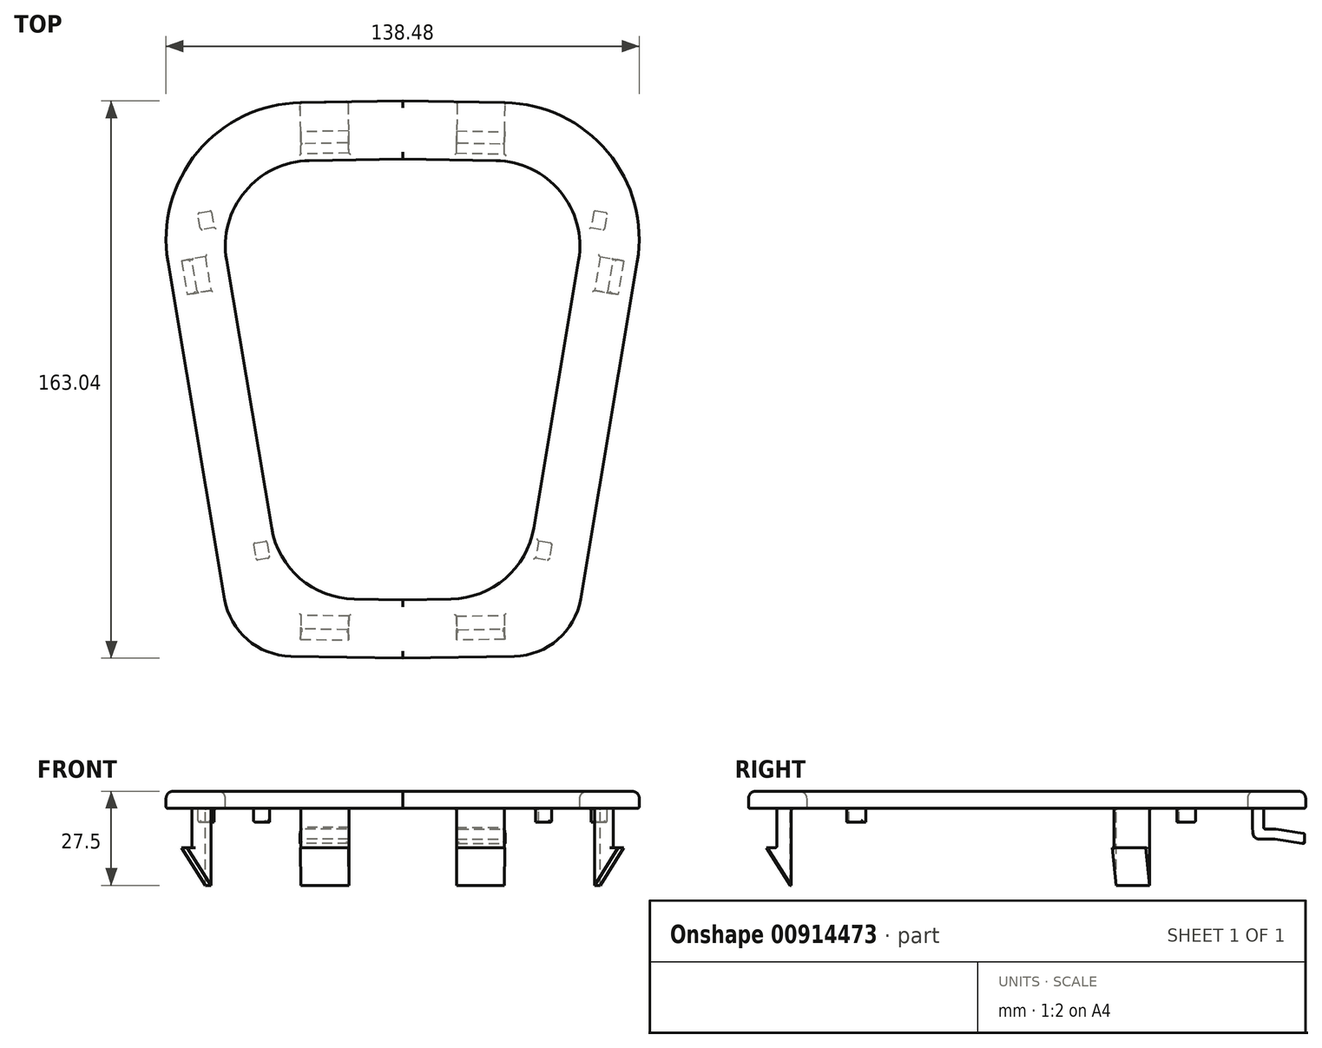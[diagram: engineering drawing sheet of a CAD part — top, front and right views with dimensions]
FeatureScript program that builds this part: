
annotation { "Feature Type Name" : "Feature", "Feature Type Description" : "" }
export const myFeature = defineFeature(function(context is Context, id is Id, definition is map)
    precondition{}
    {
        {
            var Q0;
            Q0=qCreatedBy(makeId("Top.planeOp"),FACE);
            var sketch = newSketch(context, id + "F0", { "sketchPlane" : qUnion([Q0])});
            skLineSegment(sketch, "E0", {"start": v(0, 81.52) * mm, "end": v(0, -81.52) * mm, "construction": true});
            skLineSegment(sketch, "E1", {"start": v(0, 81.52) * mm, "end": v(76.4, 80.19) * mm});
            skLineSegment(sketch, "E2", {"start": v(76.4, 80.19) * mm, "end": v(49.33, -80.66) * mm});
            skLineSegment(sketch, "E3", {"start": v(49.33, -80.66) * mm, "end": v(0, -81.52) * mm});
            skLineSegment(sketch, "E4", {"start": v(0, 81.52) * mm, "end": v(0, -81.52) * mm});
            skLineSegment(sketch, "E5.0", {"start": v(65.28, 80.38) * mm, "end": v(38.15, -80.86) * mm, "construction": true});
            skLineSegment(sketch, "E6", {"start": v(57.8, 35.9) * mm, "end": v(68.64, 34.08) * mm});
            skLineSegment(sketch, "E7", {"start": v(56.13, 26.04) * mm, "end": v(66.98, 24.22) * mm});
            skLineSegment(sketch, "E8", {"start": v(57.8, 35.9) * mm, "end": v(56.13, 26.04) * mm});
            skLineSegment(sketch, "E9", {"start": v(68.64, 34.08) * mm, "end": v(66.98, 24.22) * mm});
            skLineSegment(sketch, "E10", {"start": v(0, 66.52) * mm, "end": v(73.88, 65.23) * mm, "construction": true});
            skLineSegment(sketch, "E11", {"start": v(29.74, 66) * mm, "end": v(30, 81) * mm});
            skLineSegment(sketch, "E12", {"start": v(15.74, 66.24) * mm, "end": v(16, 81.24) * mm});
            skLineSegment(sketch, "E13", {"start": v(15.74, 66.24) * mm, "end": v(29.74, 66) * mm});
            skLineSegment(sketch, "E14", {"start": v(16, 81.24) * mm, "end": v(30, 81) * mm});
            skLineSegment(sketch, "E15", {"start": v(0, -69.52) * mm, "end": v(51.36, -68.62) * mm, "construction": true});
            skLineSegment(sketch, "E16", {"start": v(15.74, -69.25) * mm, "end": v(15.95, -81.24) * mm});
            skLineSegment(sketch, "E17", {"start": v(15.74, -69.25) * mm, "end": v(29.74, -69) * mm});
            skLineSegment(sketch, "E18", {"start": v(29.74, -69) * mm, "end": v(29.95, -81) * mm});
            skLineSegment(sketch, "E19", {"start": v(29.95, -81) * mm, "end": v(15.95, -81.24) * mm});
            skLineSegment(sketch, "E20", {"start": v(59.12, 43.8) * mm, "end": v(69.97, 41.97) * mm});
            skLineSegment(sketch, "E21", {"start": v(59.12, 43.8) * mm, "end": v(59.95, 48.73) * mm});
            skLineSegment(sketch, "E22", {"start": v(59.95, 48.73) * mm, "end": v(70.8, 46.9) * mm});
            skLineSegment(sketch, "E23", {"start": v(70.8, 46.9) * mm, "end": v(69.97, 41.97) * mm});
            skLineSegment(sketch, "E24", {"start": v(43.69, -47.92) * mm, "end": v(54.54, -49.74) * mm});
            skLineSegment(sketch, "E25", {"start": v(43.69, -47.92) * mm, "end": v(42.86, -52.85) * mm});
            skLineSegment(sketch, "E26", {"start": v(42.86, -52.85) * mm, "end": v(53.7, -54.67) * mm});
            skLineSegment(sketch, "E27", {"start": v(53.7, -54.67) * mm, "end": v(54.54, -49.74) * mm});
            skLineSegment(sketch, "E28.0", {"start": v(69.32, 80.31) * mm, "end": v(42.21, -80.78) * mm, "construction": true});
            skLineSegment(sketch, "E29.0", {"start": v(0, 69.52) * mm, "end": v(74.39, 68.22) * mm, "construction": true});
            skLineSegment(sketch, "E30.0", {"start": v(34.91, -63.9) * mm, "end": v(0, -64.52) * mm});
            skLineSegment(sketch, "E30.1", {"start": v(56.36, 63.54) * mm, "end": v(34.91, -63.9) * mm});
            skLineSegment(sketch, "E30.2", {"start": v(0, 64.52) * mm, "end": v(56.36, 63.54) * mm});
            skLineSegment(sketch, "E31", {"start": v(60.08, 25.38) * mm, "end": v(61.74, 35.24) * mm});
            skLineSegment(sketch, "E32", {"start": v(59.95, 48.73) * mm, "end": v(56, 49.39) * mm});
            skLineSegment(sketch, "E33", {"start": v(56, 49.39) * mm, "end": v(55.18, 44.46) * mm});
            skLineSegment(sketch, "E34", {"start": v(55.18, 44.46) * mm, "end": v(59.12, 43.8) * mm});
            skLineSegment(sketch, "E35", {"start": v(43.69, -47.92) * mm, "end": v(39.74, -47.25) * mm});
            skLineSegment(sketch, "E36", {"start": v(39.74, -47.25) * mm, "end": v(38.91, -52.18) * mm});
            skLineSegment(sketch, "E37", {"start": v(38.91, -52.18) * mm, "end": v(42.86, -52.85) * mm});
            skLineSegment(sketch, "E38", {"start": v(0, -73.52) * mm, "end": v(50.68, -72.64) * mm, "construction": true});
            skLineSegment(sketch, "E39", {"start": v(15.8, -73.24) * mm, "end": v(29.8, -73) * mm});
            skLineSegment(sketch, "E40", {"start": v(15.8, 69.24) * mm, "end": v(29.8, 69) * mm});
            skLineSegment(sketch, "E41", {"start": v(-105.5, -148.71) * mm, "end": v(-104.92, -148.71) * mm});
            skLineSegment(sketch, "E42", {"start": v(-104.92, -148.71) * mm, "end": v(-104.92, 145.13) * mm, "construction": true});
            skPoint(sketch, "E43", {"position": v(-104.92, 80.88) * mm});
            skPoint(sketch, "E44", {"position": v(-104.92, -81.12) * mm});
            skSolve(sketch);
        }
        {
            var Q0;
            {var subQ6=sQuery(id+"F0.wireOp",EDGE,"E8");Q0=makeQuery(id+"F0.imprint","IMPRINT",FACE,{"disambiguationData":[TD([[makeQuery(id+"F0.imprint","IMPRINT",EDGE,{"derivedFrom":subQ6}),-1.0]])]});}
            var Q1;
            {var subQ5=sQuery(id+"F0.wireOp",EDGE,"E40");var subQ8=makeQuery(id+"F0.imprint","IMPRINT",EDGE,{"derivedFrom":subQ5});var subQ9=sQuery(id+"F0.wireOp",EDGE,"E13");Q1=qUnion([makeQuery(id+"F0.imprint","IMPRINT",FACE,{"disambiguationData":[TD([[makeQuery(id+"F0.imprint","IMPRINT",EDGE,{"derivedFrom":subQ9}),1.0]])]}),makeQuery(id+"F0.imprint","IMPRINT",FACE,{"disambiguationData":[TD([[subQ8,1.0]])]})]);}
            var Q2;
            {var subQ0=sQuery(id+"F0.wireOp",EDGE,"E20");Q2=makeQuery(id+"F0.imprint","IMPRINT",FACE,{"disambiguationData":[TD([[makeQuery(id+"F0.imprint","IMPRINT",EDGE,{"derivedFrom":subQ0}),1.0]])]});}
            var Q3;
            {var subQ5=sQuery(id+"F0.wireOp",EDGE,"E31");Q3=makeQuery(id+"F0.imprint","IMPRINT",FACE,{"disambiguationData":[TD([[makeQuery(id+"F0.imprint","IMPRINT",EDGE,{"derivedFrom":subQ5}),-1.0]])]});}
            var Q4;
            {var subQ0=sQuery(id+"F0.wireOp",EDGE,"E39");var subQ3=sQuery(id+"F0.wireOp",EDGE,"E17");var subQ4=makeQuery(id+"F0.imprint","IMPRINT",EDGE,{"derivedFrom":subQ0});Q4=qUnion([makeQuery(id+"F0.imprint","IMPRINT",FACE,{"disambiguationData":[TD([[subQ4,-1.0]])]}),makeQuery(id+"F0.imprint","IMPRINT",FACE,{"disambiguationData":[TD([[makeQuery(id+"F0.imprint","IMPRINT",EDGE,{"derivedFrom":subQ3}),-1.0]])]})]);}
            var Q5;
            {var subQ0=sQuery(id+"F0.wireOp",EDGE,"E24");Q5=makeQuery(id+"F0.imprint","IMPRINT",FACE,{"disambiguationData":[TD([[makeQuery(id+"F0.imprint","IMPRINT",EDGE,{"derivedFrom":subQ0}),-1.0]])]});}
            var Q6;
            Q6=makeQuery(id+"F0.imprint","IMPRINT",FACE,{"disambiguationData":[TD([[makeQuery(id+"F0.imprint","IMPRINT",EDGE,{"derivedFrom":sQuery(id+"F0.wireOp",EDGE,"E25")}),-1.0]])]});
            var Q7;
            Q7=makeQuery(id+"F0.imprint","IMPRINT",FACE,{"disambiguationData":[TD([[makeQuery(id+"F0.imprint","IMPRINT",EDGE,{"derivedFrom":sQuery(id+"F0.wireOp",EDGE,"E21")}),1.0]])]});
            var Q8;
            {var subQ2=sQuery(id+"F0.wireOp",EDGE,"E8");Q8=makeQuery(id+"F0.imprint","IMPRINT",FACE,{"disambiguationData":[TD([[makeQuery(id+"F0.imprint","IMPRINT",EDGE,{"derivedFrom":subQ2}),1.0]])]});}
            extrude(context, id + "F1", {"entities" : qUnion([Q0, Q1, Q2, Q3, Q4, Q5, Q6, Q7, Q8]), "depth" : 5 * mm, "offsetDistance" : 25 * mm});
        }
        {
            var Q0;
            {var subQ2=sQuery(id+"F0.wireOp",EDGE,"E17");Q0=makeQuery(id+"F0.imprint","IMPRINT",FACE,{"disambiguationData":[TD([[makeQuery(id+"F0.imprint","IMPRINT",EDGE,{"derivedFrom":subQ2}),-1.0]])]});}
            var Q1;
            {var subQ2=sQuery(id+"F0.wireOp",EDGE,"E8");Q1=makeQuery(id+"F0.imprint","IMPRINT",FACE,{"disambiguationData":[TD([[makeQuery(id+"F0.imprint","IMPRINT",EDGE,{"derivedFrom":subQ2}),1.0]])]});}
            extrude(context, id + "F2", {"entities" : qUnion([Q0, Q1]), "operationType" : NewBodyOperationType.ADD, "oppositeDirection" : true, "depth" : 11.5 * mm, "offsetDistance" : 25 * mm});
        }
        {
            var Q0;
            Q0=makeQuery(id+"F2.opExtrude","SWEPT_FACE",FACE,{"disambiguationData":[OSD([sQuery(id+"F0.wireOp",EDGE,"E16")])]});
            var sketch = newSketch(context, id + "F3", { "sketchPlane" : qUnion([Q0])});
            skLineSegment(sketch, "E45", {"start": v(69.5, -11.5) * mm, "end": v(76.5, -11.5) * mm});
            skLineSegment(sketch, "E46", {"start": v(76.5, -11.5) * mm, "end": v(69.5, -22.5) * mm});
            skLineSegment(sketch, "E47", {"start": v(69.5, -22.5) * mm, "end": v(69.5, -11.5) * mm});
            skSolve(sketch);
        }
        {
            var Q0;
            Q0 = qSketchRegion(id + "F3", true);
            var Q1;
            Q1=makeQuery(id+"F2.opExtrude","SWEPT_FACE",FACE,{"disambiguationData":[OSD([sQuery(id+"F0.wireOp",EDGE,"E18")])]});
            extrude(context, id + "F4", {"entities" : qUnion([Q0]), "operationType" : NewBodyOperationType.ADD, "endBound" : BoundingType.UP_TO_SURFACE, "oppositeDirection" : true, "depth" : 25 * mm, "endBoundEntityFace" : qUnion([Q1]), "offsetDistance" : 25 * mm});
        }
        {
            var Q0;
            Q0=makeQuery(id+"F2.opExtrude","SWEPT_FACE",FACE,{"disambiguationData":[OSD([sQuery(id+"F0.wireOp",EDGE,"E7")])]});
            var sketch = newSketch(context, id + "F5", { "sketchPlane" : qUnion([Q0])});
            skLineSegment(sketch, "E48", {"start": v(51.03, -11.5) * mm, "end": v(58.03, -11.5) * mm});
            skLineSegment(sketch, "E49", {"start": v(58.03, -11.5) * mm, "end": v(51.03, -22.5) * mm});
            skLineSegment(sketch, "E50", {"start": v(51.03, -22.5) * mm, "end": v(51.03, -11.5) * mm});
            skSolve(sketch);
        }
        {
            var Q0;
            Q0 = qSketchRegion(id + "F5", true);
            var Q1;
            Q1=makeQuery(id+"F2.opExtrude","SWEPT_FACE",FACE,{"disambiguationData":[OSD([sQuery(id+"F0.wireOp",EDGE,"E6")])]});
            extrude(context, id + "F6", {"entities" : qUnion([Q0]), "operationType" : NewBodyOperationType.ADD, "endBound" : BoundingType.UP_TO_SURFACE, "oppositeDirection" : true, "depth" : 25 * mm, "endBoundEntityFace" : qUnion([Q1]), "offsetDistance" : 25 * mm});
        }
        {
            var Q0;
            {var subQ2=sQuery(id+"F0.wireOp",EDGE,"E13");Q0=makeQuery(id+"F0.imprint","IMPRINT",FACE,{"disambiguationData":[TD([[makeQuery(id+"F0.imprint","IMPRINT",EDGE,{"derivedFrom":subQ2}),1.0]])]});}
            extrude(context, id + "F7", {"entities" : qUnion([Q0]), "operationType" : NewBodyOperationType.ADD, "oppositeDirection" : true, "depth" : 5.5 * mm, "offsetDistance" : 25 * mm});
        }
        {
            var Q0;
            Q0=makeQuery(id+"F7.opExtrude","SWEPT_FACE",FACE,{"disambiguationData":[OSD([sQuery(id+"F0.wireOp",EDGE,"E11")])]});
            var sketch = newSketch(context, id + "F8", { "sketchPlane" : qUnion([Q0])});
            skLineSegment(sketch, "E51", {"start": v(66.5, -5.5) * mm, "end": v(66.54, -7.03) * mm});
            skLineSegment(sketch, "E52", {"start": v(73, -9) * mm, "end": v(81.5, -10.35) * mm});
            skLineSegment(sketch, "E53", {"start": v(81.5, -10.35) * mm, "end": v(81.5, -7.35) * mm});
            skLineSegment(sketch, "E54", {"start": v(69.5, -5.5) * mm, "end": v(69.5, -5.5) * mm});
            skPoint(sketch, "E55.visualSharp", {"position": v(69.5, -6.59) * mm});
            skLineSegment(sketch, "E56", {"start": v(70, -6) * mm, "end": v(73, -6) * mm});
            skLineSegment(sketch, "E57", {"start": v(73, -6) * mm, "end": v(81.5, -7.35) * mm});
            skLineSegment(sketch, "E58", {"start": v(66.5, -5.5) * mm, "end": v(69.5, -5.5) * mm});
            skPoint(sketch, "E59.visualSharp", {"position": v(69.5, -6) * mm});
            skArc(sketch, "E59.filletArc", {"start": v(69.5, -5.5) * mm, "mid": v(69.66, -5.85) * mm, "end": v(70, -6) * mm});
            skLineSegment(sketch, "E60", {"start": v(73, -9) * mm, "end": v(68.54, -9) * mm});
            skPoint(sketch, "E61.visualSharp", {"position": v(66.57, -9) * mm});
            skArc(sketch, "E61.filletArc", {"start": v(66.54, -7.03) * mm, "mid": v(67.13, -8.43) * mm, "end": v(68.54, -9) * mm});
            skSolve(sketch);
        }
        {
            var Q0;
            Q0 = qSketchRegion(id + "F8", true);
            var Q1;
            Q1=makeQuery(id+"F7.opExtrude","SWEPT_FACE",FACE,{"disambiguationData":[OSD([sQuery(id+"F0.wireOp",EDGE,"E12")])]});
            extrude(context, id + "F9", {"entities" : qUnion([Q0]), "operationType" : NewBodyOperationType.ADD, "endBound" : BoundingType.UP_TO_SURFACE, "oppositeDirection" : true, "depth" : 25 * mm, "endBoundEntityFace" : qUnion([Q1]), "offsetDistance" : 25 * mm});
        }
        {
            var Q0;
            Q0=makeQuery(id+"F0.imprint","IMPRINT",FACE,{"disambiguationData":[TD([[makeQuery(id+"F0.imprint","IMPRINT",EDGE,{"derivedFrom":sQuery(id+"F0.wireOp",EDGE,"E25")}),-1.0]])]});
            var Q1;
            Q1=makeQuery(id+"F0.imprint","IMPRINT",FACE,{"disambiguationData":[TD([[makeQuery(id+"F0.imprint","IMPRINT",EDGE,{"derivedFrom":sQuery(id+"F0.wireOp",EDGE,"E21")}),1.0]])]});
            extrude(context, id + "F10", {"entities" : qUnion([Q0, Q1]), "operationType" : NewBodyOperationType.ADD, "oppositeDirection" : true, "depth" : 4 * mm, "offsetDistance" : 25 * mm});
        }
        {
            var Q0;
            Q0=makeQuery(id+"F1.opExtrude","SWEPT_EDGE",EDGE,{"disambiguationData":[OSD([sQuery(id+"F0.wireOp",EDGE,"E2"),sQuery(id+"F0.wireOp",EDGE,"E3")])]});
            fillet(context, id + "F11", {"entities" : qUnion([Q0]), "radius" : 20 * mm, "tangentPropagation" : true, "allowEdgeOverflow" : false});
        }
        {
            var Q0;
            Q0=makeQuery(id+"F1.opExtrude","SWEPT_EDGE",EDGE,{"disambiguationData":[OSD([sQuery(id+"F0.wireOp",EDGE,"E1"),sQuery(id+"F0.wireOp",EDGE,"E2")])]});
            fillet(context, id + "F12", {"entities" : qUnion([Q0]), "radius" : 40 * mm, "tangentPropagation" : true, "allowEdgeOverflow" : false});
        }
        {
            var Q0;
            Q0=makeQuery(id+"F1.opExtrude","SWEPT_EDGE",EDGE,{"disambiguationData":[OSD([sQuery(id+"F0.wireOp",EDGE,"E30.0"),sQuery(id+"F0.wireOp",EDGE,"E30.1")])]});
            var Q1;
            Q1=makeQuery(id+"F1.opExtrude","SWEPT_EDGE",EDGE,{"disambiguationData":[OSD([sQuery(id+"F0.wireOp",EDGE,"E30.1"),sQuery(id+"F0.wireOp",EDGE,"E30.2")])]});
            fillet(context, id + "F13", {"entities" : qUnion([Q0, Q1]), "radius" : 25 * mm, "tangentPropagation" : true, "allowEdgeOverflow" : false});
        }
        {
            var Q0;
            Q0=makeQuery(id+"F1.opExtrude","SWEPT_BODY",BODY,{"disambiguationData":[OSD([sQuery(id+"F0.wireOp",EDGE,"E1"),sQuery(id+"F0.wireOp",EDGE,"E2"),sQuery(id+"F0.wireOp",EDGE,"E3"),sQuery(id+"F0.wireOp",EDGE,"E4"),sQuery(id+"F0.wireOp",EDGE,"E30.0"),sQuery(id+"F0.wireOp",EDGE,"E30.1"),sQuery(id+"F0.wireOp",EDGE,"E30.2")])]});
            var Q1;
            {var subQ0=sQuery(id+"F0.wireOp",EDGE,"E4");Q1=makeQuery(id+"F1.opExtrude","SWEPT_FACE",FACE,{"disambiguationData":[OSD([subQ0]),TDD([makeQuery(id+"F0.imprint","IMPRINT",EDGE,{"disambiguationData":[TD([[makeQuery(id+"F0.imprint","INTERSECT",VERTEX,{"derivedFrom":[subQ0,sQuery(id+"F0.wireOp",EDGE,"E30.2")]}),1.0]])],"derivedFrom":subQ0})])]});}
            mirror(context, id + "F14", {"operationType" : NewBodyOperationType.ADD, "entities" : qUnion([Q0]), "mirrorPlane" : qUnion([Q1])});
        }
        {
            var Q0;
            {var subQ0=makeQuery(id+"F1.opExtrude","CAP_FACE",FACE,{"disambiguationData":[OSD([sQuery(id+"F0.wireOp",EDGE,"E1"),sQuery(id+"F0.wireOp",EDGE,"E2"),sQuery(id+"F0.wireOp",EDGE,"E3"),sQuery(id+"F0.wireOp",EDGE,"E4"),sQuery(id+"F0.wireOp",EDGE,"E30.0"),sQuery(id+"F0.wireOp",EDGE,"E30.1"),sQuery(id+"F0.wireOp",EDGE,"E30.2")])],"isStart":false});Q0=makeQuery(id+"F14.boolean.opBoolean","MERGE",FACE,{"derivedFrom":[subQ0,makeQuery(id+"F14.opPattern","COPY",FACE,{"derivedFrom":subQ0,"instanceName":"1"})]});}
            fillet(context, id + "F15", {"entities" : qUnion([Q0]), "radius" : 2 * mm, "tangentPropagation" : true, "allowEdgeOverflow" : false});
        }
        {
            var Q0;
            {var subQ0=makeQuery(id+"F1.opExtrude","CAP_FACE",FACE,{"disambiguationData":[OSD([sQuery(id+"F0.wireOp",EDGE,"E1"),sQuery(id+"F0.wireOp",EDGE,"E2"),sQuery(id+"F0.wireOp",EDGE,"E3"),sQuery(id+"F0.wireOp",EDGE,"E4"),sQuery(id+"F0.wireOp",EDGE,"E30.0"),sQuery(id+"F0.wireOp",EDGE,"E30.1"),sQuery(id+"F0.wireOp",EDGE,"E30.2")])],"isStart":true});Q0=makeQuery(id+"F14.boolean.opBoolean","MERGE",FACE,{"derivedFrom":[subQ0,makeQuery(id+"F14.opPattern","COPY",FACE,{"derivedFrom":subQ0,"instanceName":"1"})]});}
            var Q1;
            Q1=makeQuery(id+"F14.opPattern","COPY",FACE,{"derivedFrom":makeQuery(id+"F2.opExtrude","SWEPT_FACE",FACE,{"disambiguationData":[OSD([sQuery(id+"F0.wireOp",EDGE,"E39")])]}),"instanceName":"1"});
            var Q2;
            Q2=makeQuery(id+"F2.opExtrude","SWEPT_FACE",FACE,{"disambiguationData":[OSD([sQuery(id+"F0.wireOp",EDGE,"E39")])]});
            var Q3;
            Q3=makeQuery(id+"F10.opExtrude","SWEPT_FACE",FACE,{"disambiguationData":[OSD([sQuery(id+"F0.wireOp",EDGE,"E25")])]});
            var Q4;
            Q4=makeQuery(id+"F2.opExtrude","SWEPT_FACE",FACE,{"disambiguationData":[OSD([sQuery(id+"F0.wireOp",EDGE,"E31")])]});
            var Q5;
            Q5=makeQuery(id+"F10.opExtrude","SWEPT_FACE",FACE,{"disambiguationData":[OSD([sQuery(id+"F0.wireOp",EDGE,"E21")])]});
            var Q6;
            Q6=makeQuery(id+"F10.opExtrude","SWEPT_FACE",FACE,{"disambiguationData":[OSD([sQuery(id+"F0.wireOp",EDGE,"E32")])]});
            var Q7;
            Q7=makeQuery(id+"F7.opExtrude","SWEPT_FACE",FACE,{"disambiguationData":[OSD([sQuery(id+"F0.wireOp",EDGE,"E40")])]});
            var Q8;
            Q8=makeQuery(id+"F9.opExtrude","SWEPT_FACE",FACE,{"disambiguationData":[OSD([sQuery(id+"F8.wireOp",EDGE,"E53")])]});
            var Q9;
            Q9=makeQuery(id+"F9.opExtrude","SWEPT_FACE",FACE,{"disambiguationData":[OSD([sQuery(id+"F8.wireOp",EDGE,"E57")])]});
            var Q10;
            Q10=makeQuery(id+"F14.opPattern","COPY",FACE,{"derivedFrom":makeQuery(id+"F7.opExtrude","SWEPT_FACE",FACE,{"disambiguationData":[OSD([sQuery(id+"F0.wireOp",EDGE,"E40")])]}),"instanceName":"1"});
            var Q11;
            Q11=makeQuery(id+"F14.opPattern","COPY",FACE,{"derivedFrom":makeQuery(id+"F9.opExtrude","SWEPT_FACE",FACE,{"disambiguationData":[OSD([sQuery(id+"F8.wireOp",EDGE,"E53")])]}),"instanceName":"1"});
            var Q12;
            Q12=makeQuery(id+"F14.opPattern","COPY",FACE,{"derivedFrom":makeQuery(id+"F9.opExtrude","SWEPT_FACE",FACE,{"disambiguationData":[OSD([sQuery(id+"F8.wireOp",EDGE,"E57")])]}),"instanceName":"1"});
            var Q13;
            Q13=makeQuery(id+"F14.opPattern","COPY",FACE,{"derivedFrom":makeQuery(id+"F10.opExtrude","SWEPT_FACE",FACE,{"disambiguationData":[OSD([sQuery(id+"F0.wireOp",EDGE,"E21")])]}),"instanceName":"1"});
            var Q14;
            Q14=makeQuery(id+"F14.opPattern","COPY",FACE,{"derivedFrom":makeQuery(id+"F10.opExtrude","SWEPT_FACE",FACE,{"disambiguationData":[OSD([sQuery(id+"F0.wireOp",EDGE,"E32")])]}),"instanceName":"1"});
            var Q15;
            Q15=makeQuery(id+"F14.opPattern","COPY",FACE,{"derivedFrom":makeQuery(id+"F2.opExtrude","SWEPT_FACE",FACE,{"disambiguationData":[OSD([sQuery(id+"F0.wireOp",EDGE,"E31")])]}),"instanceName":"1"});
            var Q16;
            Q16=makeQuery(id+"F14.opPattern","COPY",FACE,{"derivedFrom":makeQuery(id+"F10.opExtrude","SWEPT_FACE",FACE,{"disambiguationData":[OSD([sQuery(id+"F0.wireOp",EDGE,"E25")])]}),"instanceName":"1"});
            var Q17;
            Q17=makeQuery(id+"F14.opPattern","COPY",FACE,{"derivedFrom":makeQuery(id+"F10.opExtrude","SWEPT_FACE",FACE,{"disambiguationData":[OSD([sQuery(id+"F0.wireOp",EDGE,"E37")])]}),"instanceName":"1"});
            var Q18;
            Q18=makeQuery(id+"F14.opPattern","COPY",FACE,{"derivedFrom":makeQuery(id+"F10.opExtrude","SWEPT_FACE",FACE,{"disambiguationData":[OSD([sQuery(id+"F0.wireOp",EDGE,"E35")])]}),"instanceName":"1"});
            fillet(context, id + "F16", {"entities" : qUnion([Q0, Q1, Q2, Q3, Q4, Q5, Q6, Q7, Q8, Q9, Q10, Q11, Q12, Q13, Q14, Q15, Q16, Q17, Q18]), "radius" : 0.5 * mm, "tangentPropagation" : true, "allowEdgeOverflow" : false});
        }
    });
